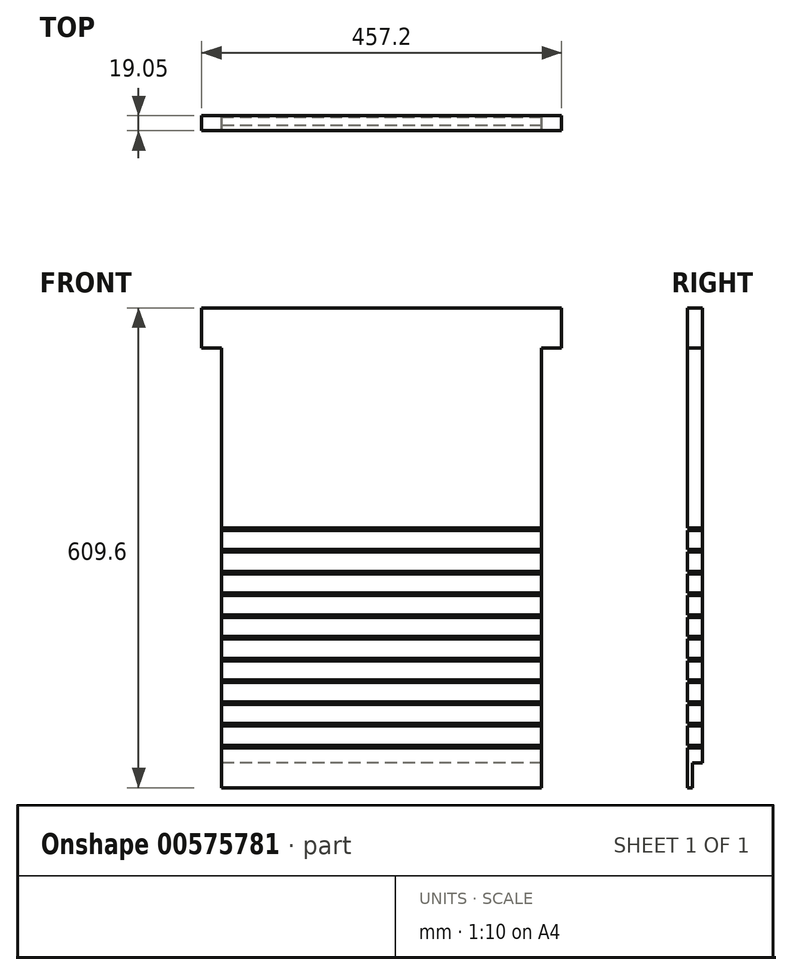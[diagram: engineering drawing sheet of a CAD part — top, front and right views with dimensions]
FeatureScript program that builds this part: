
annotation { "Feature Type Name" : "Feature", "Feature Type Description" : "" }
export const myFeature = defineFeature(function(context is Context, id is Id, definition is map)
    precondition{}
    {
        {
            var Q0;
            Q0=qCreatedBy(makeId("Front.planeOp"),FACE);
            var sketch = newSketch(context, id + "F0", { "sketchPlane" : qUnion([Q0])});
            skLineSegment(sketch, "E0", {"start": v(218.02, 487.6) * mm, "end": v(218.02, -71.2) * mm});
            skLineSegment(sketch, "E1", {"start": v(218.02, -71.2) * mm, "end": v(-188.38, -71.2) * mm});
            skLineSegment(sketch, "E2", {"start": v(-188.38, -71.2) * mm, "end": v(-188.38, 487.6) * mm});
            skLineSegment(sketch, "E3", {"start": v(-188.38, 487.6) * mm, "end": v(-213.78, 487.6) * mm});
            skLineSegment(sketch, "E4", {"start": v(-213.78, 487.6) * mm, "end": v(-213.78, 538.4) * mm});
            skLineSegment(sketch, "E5", {"start": v(-213.78, 538.4) * mm, "end": v(243.42, 538.4) * mm});
            skLineSegment(sketch, "E6", {"start": v(243.42, 538.4) * mm, "end": v(243.42, 487.6) * mm});
            skLineSegment(sketch, "E7", {"start": v(243.42, 487.6) * mm, "end": v(218.02, 487.6) * mm});
            skSolve(sketch);
        }
        {
            var Q0;
            Q0 = qSketchRegion(id + "F0", true);
            extrude(context, id + "F1", {"entities" : qUnion([Q0]), "depth" : 19.05 * mm, "offsetDistance" : 25.4 * mm});
        }
        {
            var Q0;
            Q0=makeQuery(id+"F1.opExtrude","CAP_FACE",FACE,{"disambiguationData":[OSD([sQuery(id+"F0.wireOp",EDGE,"E0"),sQuery(id+"F0.wireOp",EDGE,"E1"),sQuery(id+"F0.wireOp",EDGE,"E2"),sQuery(id+"F0.wireOp",EDGE,"E3"),sQuery(id+"F0.wireOp",EDGE,"E4"),sQuery(id+"F0.wireOp",EDGE,"E5"),sQuery(id+"F0.wireOp",EDGE,"E6"),sQuery(id+"F0.wireOp",EDGE,"E7")])],"isStart":false});
            var sketch = newSketch(context, id + "F2", { "sketchPlane" : qUnion([Q0])});
            skLineSegment(sketch, "E8", {"start": v(-188.38, -20.4) * mm, "end": v(218.02, -20.4) * mm});
            skLineSegment(sketch, "E9", {"start": v(-188.38, 259) * mm, "end": v(218.02, 259) * mm});
            skLineSegment(sketch, "E10", {"start": v(-188.38, -17.22) * mm, "end": v(218.02, -17.22) * mm});
            skLineSegment(sketch, "E11", {"start": v(218.02, 255.83) * mm, "end": v(-188.38, 255.83) * mm});
            skLineSegment(sketch, "E12", {"start": v(218.02, 7.22) * mm, "end": v(-188.38, 7.22) * mm});
            skLineSegment(sketch, "E13", {"start": v(-188.38, 10.4) * mm, "end": v(218.02, 10.4) * mm});
            skLineSegment(sketch, "E14", {"start": v(218.02, 62.47) * mm, "end": v(-188.38, 62.47) * mm});
            skLineSegment(sketch, "E15", {"start": v(-188.38, 65.64) * mm, "end": v(218.02, 65.64) * mm});
            skLineSegment(sketch, "E16", {"start": v(218.02, 90.1) * mm, "end": v(-188.38, 90.1) * mm});
            skLineSegment(sketch, "E17", {"start": v(-188.38, 93.27) * mm, "end": v(218.02, 93.27) * mm});
            skLineSegment(sketch, "E18", {"start": v(218.02, 117.71) * mm, "end": v(-188.38, 117.71) * mm});
            skLineSegment(sketch, "E19", {"start": v(-188.38, 120.89) * mm, "end": v(218.02, 120.89) * mm});
            skLineSegment(sketch, "E20", {"start": v(218.02, 145.34) * mm, "end": v(-188.38, 145.34) * mm});
            skLineSegment(sketch, "E21", {"start": v(-188.38, 148.51) * mm, "end": v(218.02, 148.51) * mm});
            skLineSegment(sketch, "E22", {"start": v(218.02, 172.96) * mm, "end": v(-188.38, 172.96) * mm});
            skLineSegment(sketch, "E23", {"start": v(-188.38, 176.13) * mm, "end": v(218.02, 176.13) * mm});
            skLineSegment(sketch, "E24", {"start": v(218.02, 200.58) * mm, "end": v(-188.38, 200.58) * mm});
            skLineSegment(sketch, "E25", {"start": v(-188.38, 203.76) * mm, "end": v(218.02, 203.76) * mm});
            skLineSegment(sketch, "E26", {"start": v(218.02, 228.2) * mm, "end": v(-188.38, 228.2) * mm});
            skLineSegment(sketch, "E27", {"start": v(-188.38, 231.38) * mm, "end": v(218.02, 231.38) * mm});
            skLineSegment(sketch, "E28", {"start": v(-188.38, 252.65) * mm, "end": v(218.02, 252.65) * mm});
            skLineSegment(sketch, "E29", {"start": v(-188.38, 255.83) * mm, "end": v(-188.38, 231.38) * mm});
            skLineSegment(sketch, "E30", {"start": v(-188.38, 228.2) * mm, "end": v(-188.38, 252.65) * mm});
            skLineSegment(sketch, "E31", {"start": v(-188.38, 228.2) * mm, "end": v(-188.38, 203.76) * mm});
            skLineSegment(sketch, "E32", {"start": v(-188.38, 200.58) * mm, "end": v(-188.38, 176.13) * mm});
            skLineSegment(sketch, "E33", {"start": v(-188.38, 172.96) * mm, "end": v(-188.38, 148.51) * mm});
            skLineSegment(sketch, "E34", {"start": v(-188.38, 145.34) * mm, "end": v(-188.38, 120.89) * mm});
            skLineSegment(sketch, "E35", {"start": v(-188.38, 117.71) * mm, "end": v(-188.38, 93.27) * mm});
            skLineSegment(sketch, "E36", {"start": v(-188.38, 90.1) * mm, "end": v(-188.38, 65.64) * mm});
            skLineSegment(sketch, "E37", {"start": v(-188.38, 38.02) * mm, "end": v(218.02, 38.02) * mm});
            skLineSegment(sketch, "E38", {"start": v(218.02, 34.85) * mm, "end": v(-188.38, 34.85) * mm});
            skLineSegment(sketch, "E39", {"start": v(-188.38, 10.4) * mm, "end": v(-188.38, 34.85) * mm});
            skLineSegment(sketch, "E40", {"start": v(-188.38, 38.02) * mm, "end": v(-188.38, 62.47) * mm});
            skLineSegment(sketch, "E41", {"start": v(-188.38, 7.22) * mm, "end": v(-188.38, -17.22) * mm});
            skLineSegment(sketch, "E42", {"start": v(-188.38, -17.22) * mm, "end": v(-188.38, -20.4) * mm});
            skLineSegment(sketch, "E43", {"start": v(-188.38, 7.22) * mm, "end": v(-188.38, 10.4) * mm});
            skLineSegment(sketch, "E44", {"start": v(-188.38, 34.85) * mm, "end": v(-188.38, 38.02) * mm});
            skLineSegment(sketch, "E45", {"start": v(-188.38, 62.47) * mm, "end": v(-188.38, 65.64) * mm});
            skLineSegment(sketch, "E46", {"start": v(-188.38, 90.1) * mm, "end": v(-188.38, 93.27) * mm});
            skLineSegment(sketch, "E47", {"start": v(-188.38, 117.71) * mm, "end": v(-188.38, 120.89) * mm});
            skLineSegment(sketch, "E48", {"start": v(-188.38, 145.34) * mm, "end": v(-188.38, 148.51) * mm});
            skLineSegment(sketch, "E49", {"start": v(-188.38, 172.96) * mm, "end": v(-188.38, 176.13) * mm});
            skLineSegment(sketch, "E50", {"start": v(-188.38, 200.58) * mm, "end": v(-188.38, 203.76) * mm});
            skLineSegment(sketch, "E51", {"start": v(-188.38, 228.2) * mm, "end": v(-188.38, 231.38) * mm});
            skLineSegment(sketch, "E52", {"start": v(-188.38, 255.83) * mm, "end": v(-188.38, 252.65) * mm});
            skLineSegment(sketch, "E53", {"start": v(-188.38, 255.83) * mm, "end": v(-188.38, 259) * mm});
            skSolve(sketch);
        }
        {
            var Q0;
            {var subQ0=sQuery(id+"F2.wireOp",EDGE,"E9");Q0=makeQuery(id+"F2.imprint","IMPRINT",FACE,{"disambiguationData":[TD([[makeQuery(id+"F2.imprint","IMPRINT",EDGE,{"derivedFrom":subQ0}),-1.0]])]});}
            var Q1;
            {var subQ0=sQuery(id+"F2.wireOp",EDGE,"E26");Q1=makeQuery(id+"F2.imprint","IMPRINT",FACE,{"disambiguationData":[TD([[makeQuery(id+"F2.imprint","IMPRINT",EDGE,{"derivedFrom":subQ0}),-1.0]])]});}
            var Q2;
            {var subQ0=sQuery(id+"F2.wireOp",EDGE,"E11");Q2=makeQuery(id+"F2.imprint","IMPRINT",FACE,{"disambiguationData":[TD([[makeQuery(id+"F2.imprint","IMPRINT",EDGE,{"derivedFrom":subQ0}),1.0]])]});}
            var Q3;
            {var subQ0=sQuery(id+"F2.wireOp",EDGE,"E26");Q3=makeQuery(id+"F2.imprint","IMPRINT",FACE,{"disambiguationData":[TD([[makeQuery(id+"F2.imprint","IMPRINT",EDGE,{"derivedFrom":subQ0}),-1.0]])]});}
            var Q4;
            {var subQ0=sQuery(id+"F2.wireOp",EDGE,"E24");Q4=makeQuery(id+"F2.imprint","IMPRINT",FACE,{"disambiguationData":[TD([[makeQuery(id+"F2.imprint","IMPRINT",EDGE,{"derivedFrom":subQ0}),-1.0]])]});}
            var Q5;
            {var subQ0=sQuery(id+"F2.wireOp",EDGE,"E22");Q5=makeQuery(id+"F2.imprint","IMPRINT",FACE,{"disambiguationData":[TD([[makeQuery(id+"F2.imprint","IMPRINT",EDGE,{"derivedFrom":subQ0}),-1.0]])]});}
            var Q6;
            {var subQ0=sQuery(id+"F2.wireOp",EDGE,"E20");Q6=makeQuery(id+"F2.imprint","IMPRINT",FACE,{"disambiguationData":[TD([[makeQuery(id+"F2.imprint","IMPRINT",EDGE,{"derivedFrom":subQ0}),-1.0]])]});}
            var Q7;
            {var subQ0=sQuery(id+"F2.wireOp",EDGE,"E18");Q7=makeQuery(id+"F2.imprint","IMPRINT",FACE,{"disambiguationData":[TD([[makeQuery(id+"F2.imprint","IMPRINT",EDGE,{"derivedFrom":subQ0}),-1.0]])]});}
            var Q8;
            {var subQ0=sQuery(id+"F2.wireOp",EDGE,"E16");Q8=makeQuery(id+"F2.imprint","IMPRINT",FACE,{"disambiguationData":[TD([[makeQuery(id+"F2.imprint","IMPRINT",EDGE,{"derivedFrom":subQ0}),-1.0]])]});}
            var Q9;
            {var subQ0=sQuery(id+"F2.wireOp",EDGE,"E14");Q9=makeQuery(id+"F2.imprint","IMPRINT",FACE,{"disambiguationData":[TD([[makeQuery(id+"F2.imprint","IMPRINT",EDGE,{"derivedFrom":subQ0}),-1.0]])]});}
            var Q10;
            {var subQ0=sQuery(id+"F2.wireOp",EDGE,"E37");Q10=makeQuery(id+"F2.imprint","IMPRINT",FACE,{"disambiguationData":[TD([[makeQuery(id+"F2.imprint","IMPRINT",EDGE,{"derivedFrom":subQ0}),-1.0]])]});}
            var Q11;
            {var subQ0=sQuery(id+"F2.wireOp",EDGE,"E12");Q11=makeQuery(id+"F2.imprint","IMPRINT",FACE,{"disambiguationData":[TD([[makeQuery(id+"F2.imprint","IMPRINT",EDGE,{"derivedFrom":subQ0}),-1.0]])]});}
            var Q12;
            {var subQ0=sQuery(id+"F2.wireOp",EDGE,"E8");Q12=makeQuery(id+"F2.imprint","IMPRINT",FACE,{"disambiguationData":[TD([[makeQuery(id+"F2.imprint","IMPRINT",EDGE,{"derivedFrom":subQ0}),1.0]])]});}
            extrude(context, id + "F3", {"entities" : qUnion([Q0, Q1, Q2, Q3, Q4, Q5, Q6, Q7, Q8, Q9, Q10, Q11, Q12]), "operationType" : NewBodyOperationType.REMOVE, "oppositeDirection" : true, "depth" : 17.46 * mm, "offsetDistance" : 25.4 * mm});
        }
        {
            var Q0;
            Q0=makeQuery(id+"F1.opExtrude","CAP_FACE",FACE,{"disambiguationData":[OSD([sQuery(id+"F0.wireOp",EDGE,"E0"),sQuery(id+"F0.wireOp",EDGE,"E1"),sQuery(id+"F0.wireOp",EDGE,"E2"),sQuery(id+"F0.wireOp",EDGE,"E3"),sQuery(id+"F0.wireOp",EDGE,"E4"),sQuery(id+"F0.wireOp",EDGE,"E5"),sQuery(id+"F0.wireOp",EDGE,"E6"),sQuery(id+"F0.wireOp",EDGE,"E7")])],"isStart":true});
            var sketch = newSketch(context, id + "F4", { "sketchPlane" : qUnion([Q0])});
            skLineSegment(sketch, "E54", {"start": v(-218.02, -39.45) * mm, "end": v(188.38, -39.45) * mm});
            skSolve(sketch);
        }
        {
            var Q0;
            {var subQ0=sQuery(id+"F4.wireOp",EDGE,"E54");Q0=makeQuery(id+"F4.imprint","IMPRINT",FACE,{"disambiguationData":[TD([[makeQuery(id+"F4.imprint","IMPRINT",EDGE,{"derivedFrom":subQ0}),-1.0]])]});}
            extrude(context, id + "F5", {"entities" : qUnion([Q0]), "operationType" : NewBodyOperationType.REMOVE, "oppositeDirection" : true, "depth" : 12.7 * mm, "offsetDistance" : 25.4 * mm});
        }
    });
